# Revit family: 2CKA006410A0397
name_source: partatom
category: Elektroinstallationen
revit_build: Autodesk Revit 2017 (Build: 20160225_1515(x64)
units: mm (PartAtom-declared; Revit-internal decimal feet)

## family parameters
Basisbauteil = Fläche
Beim Laden mit Abzugskörper schneiden = Nein
Bemaßung runder Anschluss = Durchmesser verwenden
Beschriftungsausrichtung beibehalten = Nein
Gemeinsam genutzt = Nein
Raumberechnungspunkt = Nein
Teiletyp = Normal

## types (1)
- 2CKA006410A0397
    Aussperrsicherung = Ja
    BIM = https://media.live.bim.site
    BIMSITE_PRODUCT_ID = aaf2a1c10890495088b3242478643ab769288b65
    Befestigungsart = Klemmbefestigung
    Beschreibung = Komfort-Timer-Bedienelement, Zeitschaltuhren, Busch-Timer, Komfort-Timer-Bedienelement Für manuelles und zeitgesteuertes Schalten von Rollläden, Jalousien, Markisen, Beleuchtungen, elektrischen Verbrauchern. Mit Astroprogramm. Individuelle Astroverschiebung und Astrosperrzeit. Manuelle Bedienung der Beschattung / Beleuchtung jederzeit möglich. Einfache Einstellung über hochauflösendes Display mit Hintergrundbeleuchtung. Schaltzeiten/Datum/Uhrzeit voreingestellt. Ab Werk voreingestellte Schaltzeiten, individuelle Anpassung möglich. Automatische Sommer-/Winterzeitumstellung (abschaltbar). Schaltzeiten/Programm sind netzausfallsicher gespeichert. Gangreserve für Uhrzeit und Datum > 10 Jahre. Einfache Umschaltung für Hand-/Automatik-/Urlaubsbetrieb. In Kombination mit Busch-Jalousiecontroleinsatz II 6411 U/S-101 Sonnenschutz- und Dämmerungsfunktion. Frei einstellbare temperatur- und helligkeitsabhängige Sonnenschutzfunktion. Frei einstellbare Dämmerungsfunktion. Frei einstellbare Laufzeiten für Beschattung und Lüftung. Programmierung nur mit aufgestecktem Bedienelement unter Spannung möglich. 6 Schaltzeiten pro Tag für jeden Wochentag frei einstellbar. Astro-Schaltzeiten und Schaltzeiten sind kombinierbar. In Kombination mit LED-Dimmer 6524 U, Busch-Universal-Zentraldimmer Einsatz 6593 U oder Busch-Memory-Taststeuergerät 6550 U-101 ist die Helligkeit der Beleuchtung für jede EIN-Schaltzeit einstellbar. Für Busch-Jalousiecontrol II Einsatz 6411 U-101, 6411 U/S-101. Für Busch-Universal-Relais-Einsatz 6401 U-102. Für Busch-Universal-Zentraldimmer Einsatz 6593 U. Für LED-Dimmer-Einsatz 6524 U und 6526 U. Für Busch-Memory-Taststeuergerät 6550 U-101. Temperaturbereich Gerät: 0 °C bis 35 °C
    Datenblatt = https://media.live.bim.site
    Dämmerungswert einstellbar [lx] = [15:300]
    GTIN = 4011395186619
    Gangreserve [s] = 226800000
    Geeignet für Schutzart (IP) = IP20
    Gerätebreite [mm] = 63
    Gerätehöhe [mm] = 63
    Gewicht [kg/m] = 0.062
    Glass = Glass
    HAN = 2CKA006410A0397
    Halogenfrei = Ja
    HeinzeBIM = https://www.heinze.de
    Hersteller = Busch-Jaeger
    Integrierte Zeitschaltuhr = Ja
    Ist System = Nein
    Ist Zubehör = Nein
    Mit Astro-Programm = Ja
    Montageart = Unterputz
    Oberfläche = unbehandelt
    Produktseite = https://media.live.bim.site
    Sonnenschutzwert einstellbar [lx] = [5000:50000]
    TYPE = 6455-101
    Typname = Komfort-Timer-Bedienelement, Zeitschaltuhren, Busch-Timer
    URL = https://www.busch-jaeger.de
    Vorgabe-Ansicht = 1219 mm
    Werkstoff = Kunststoff
    Werkstoffgüte = Thermoplast
    White = White
    Zufallsgenerator = Ja
    Zusammenstellung = Bedienaufsatz

## geometry (parser evidence)
native form markers: Sweep x3
no freeform markers — native parametric forms only
